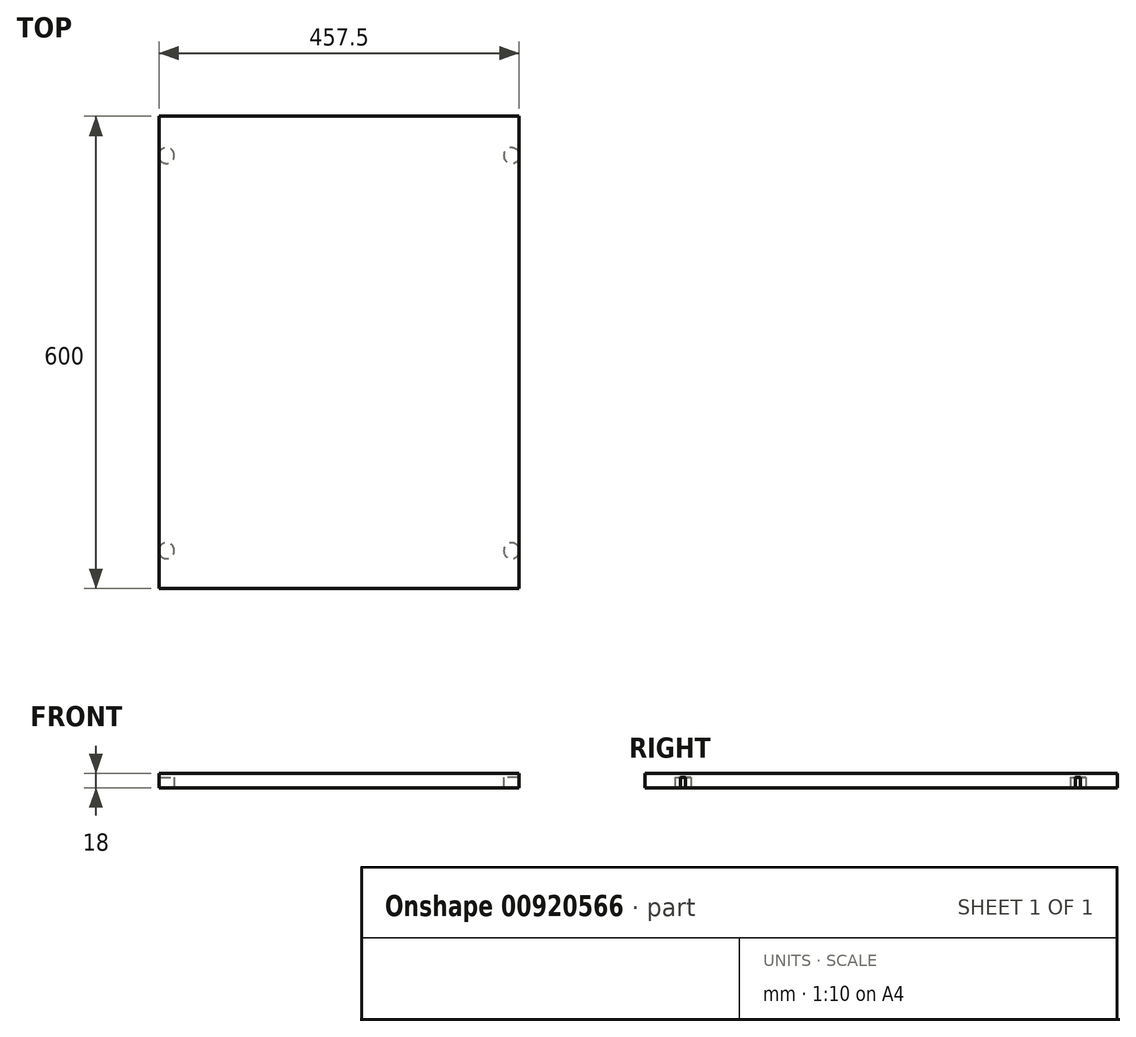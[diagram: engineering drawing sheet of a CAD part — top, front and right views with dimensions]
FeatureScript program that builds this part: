
annotation { "Feature Type Name" : "Feature", "Feature Type Description" : "" }
export const myFeature = defineFeature(function(context is Context, id is Id, definition is map)
    precondition{}
    {
        {
            var Q0;
            Q0=qCreatedBy(makeId("Top.planeOp"),FACE);
            var sketch = newSketch(context, id + "F0", { "sketchPlane" : qUnion([Q0])});
            skLineSegment(sketch, "E0.bottom", {"start": v(228.75, -300) * mm, "end": v(-228.75, -300) * mm});
            skLineSegment(sketch, "E0.top", {"start": v(228.75, 300) * mm, "end": v(-228.75, 300) * mm});
            skLineSegment(sketch, "E0.left", {"start": v(228.75, -300) * mm, "end": v(228.75, 300) * mm});
            skLineSegment(sketch, "E0.right", {"start": v(-228.75, -300) * mm, "end": v(-228.75, 300) * mm});
            skPoint(sketch, "E0.middle", {"position": v(0, 0) * mm});
            skSolve(sketch);
        }
        {
            var Q0;
            Q0=qSketchRegion(id+"F0",true);
            extrude(context, id + "F1", {"entities" : qUnion([Q0]), "depth" : 18 * mm, "offsetDistance" : 25 * mm, "symmetric" : true});
        }
        {
            var Q0;
            Q0=makeQuery(id+"F1.opExtrude","CAP_FACE",FACE,{"disambiguationData":[OSD([sQuery(id+"F0.wireOp",EDGE,"E0.bottom"),sQuery(id+"F0.wireOp",EDGE,"E0.top"),sQuery(id+"F0.wireOp",EDGE,"E0.left"),sQuery(id+"F0.wireOp",EDGE,"E0.right")])],"isStart":true});
            var sketch = newSketch(context, id + "F2", { "sketchPlane" : qUnion([Q0])});
            skCircle(sketch, "E1", {"center": v(-219.25, 252) * mm, "radius": 10 * mm});
            skCircle(sketch, "E2.0.1.0", {"center": v(-219.25, -250) * mm, "radius": 10 * mm});
            skCircle(sketch, "E2.1.0.0", {"center": v(219.25, 252) * mm, "radius": 10 * mm});
            skCircle(sketch, "E2.1.1.0", {"center": v(219.25, -250) * mm, "radius": 10 * mm});
            skLineSegment(sketch, "E2.direction2", {"start": v(-219.25, 252) * mm, "end": v(-219.25, -250) * mm, "construction": true});
            skSolve(sketch);
        }
        {
            var Q0;
            Q0=qSketchRegion(id+"F2",true);
            extrude(context, id + "F3", {"entities" : qUnion([Q0]), "operationType" : NewBodyOperationType.REMOVE, "oppositeDirection" : true, "depth" : 13 * mm, "offsetDistance" : 25 * mm});
        }
    });
